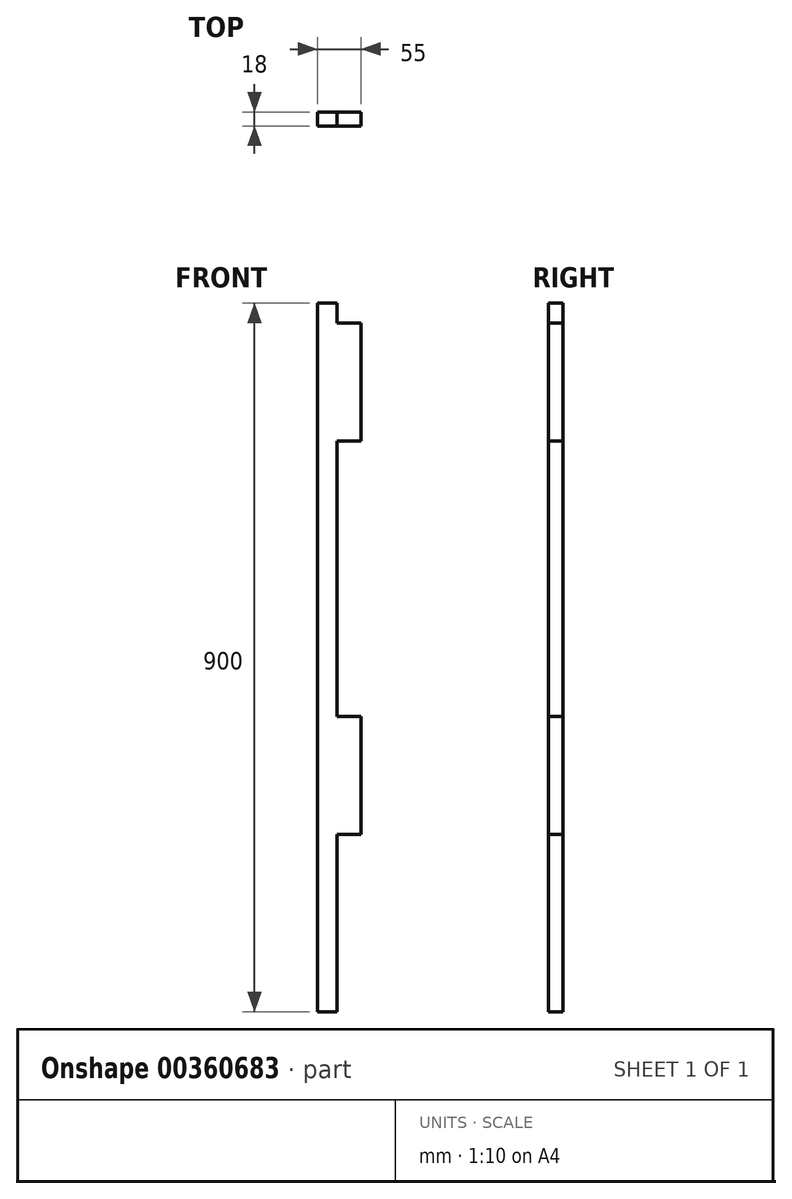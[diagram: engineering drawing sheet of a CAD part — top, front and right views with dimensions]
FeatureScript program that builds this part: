
annotation { "Feature Type Name" : "Feature", "Feature Type Description" : "" }
export const myFeature = defineFeature(function(context is Context, id is Id, definition is map)
    precondition{}
    {
        {
            var Q0;
            Q0=qCreatedBy(makeId("Front.planeOp"),FACE);
            var sketch = newSketch(context, id + "F0", { "sketchPlane" : qUnion([Q0])});
            skLineSegment(sketch, "E0.bottom", {"start": v(0, 0) * mm, "end": v(25, 0) * mm});
            skLineSegment(sketch, "E0.top", {"start": v(0, 900) * mm, "end": v(25, 900) * mm});
            skLineSegment(sketch, "E0.left", {"start": v(0, 0) * mm, "end": v(0, 900) * mm});
            skLineSegment(sketch, "E0.right", {"start": v(25, 0) * mm, "end": v(25, 225) * mm});
            skLineSegment(sketch, "E1.bottom", {"start": v(25, 875) * mm, "end": v(55, 875) * mm});
            skLineSegment(sketch, "E1.top", {"start": v(25, 725) * mm, "end": v(55, 725) * mm});
            skLineSegment(sketch, "E1.right", {"start": v(55, 875) * mm, "end": v(55, 725) * mm});
            skLineSegment(sketch, "E2.bottom", {"start": v(25, 375) * mm, "end": v(55, 375) * mm});
            skLineSegment(sketch, "E2.top", {"start": v(25, 225) * mm, "end": v(55, 225) * mm});
            skLineSegment(sketch, "E2.right", {"start": v(55, 375) * mm, "end": v(55, 225) * mm});
            skLineSegment(sketch, "E3.trimOffspring", {"start": v(25, 875) * mm, "end": v(25, 900) * mm});
            skLineSegment(sketch, "E4.trimOffspring", {"start": v(25, 375) * mm, "end": v(25, 725) * mm});
            skSolve(sketch);
        }
        {
            var Q0;
            Q0=makeQuery(id+"F0.imprint","IMPRINT",FACE,{"disambiguationData":[TD([[makeQuery(id+"F0.imprint","IMPRINT",EDGE,{"derivedFrom":sQuery(id+"F0.wireOp",EDGE,"E0.bottom")}),1.0]])]});
            extrude(context, id + "F1", {"entities" : qUnion([Q0]), "depth" : 18 * mm});
        }
    });
